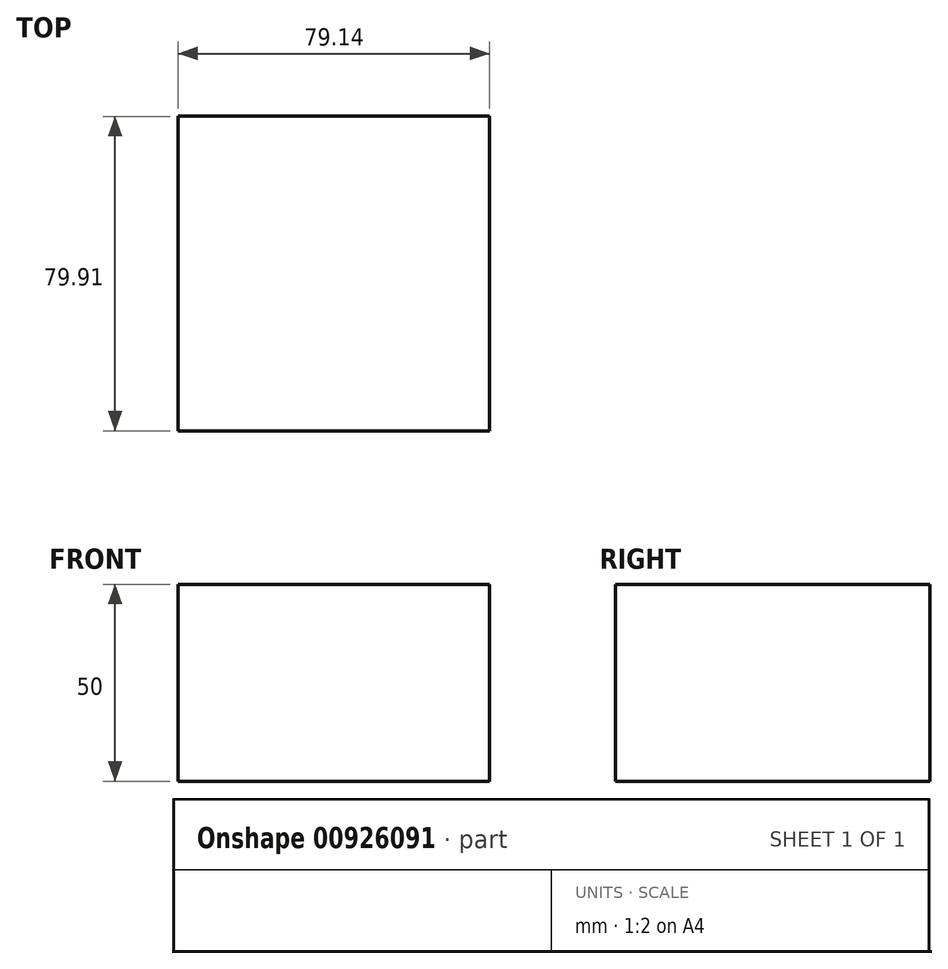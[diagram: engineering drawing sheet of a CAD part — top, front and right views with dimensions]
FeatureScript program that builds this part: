
annotation { "Feature Type Name" : "Feature", "Feature Type Description" : "" }
export const myFeature = defineFeature(function(context is Context, id is Id, definition is map)
    precondition{}
    {
        {
            var Q0;
            Q0=qCreatedBy(makeId("Top.planeOp"),FACE);
            var sketch = newSketch(context, id + "F0", { "sketchPlane" : qUnion([Q0])});
            skLineSegment(sketch, "E0.bottom", {"start": v(9.99, -15.03) * mm, "end": v(10.38, -15.03) * mm});
            skLineSegment(sketch, "E0.top", {"start": v(9.99, -19.69) * mm, "end": v(10.38, -19.69) * mm});
            skLineSegment(sketch, "E1.bottom", {"start": v(31.9, -28.6) * mm, "end": v(-47.23, -28.6) * mm});
            skLineSegment(sketch, "E1.top", {"start": v(31.9, 51.3) * mm, "end": v(-47.23, 51.3) * mm});
            skLineSegment(sketch, "E1.left", {"start": v(31.9, -28.6) * mm, "end": v(31.9, 51.3) * mm});
            skLineSegment(sketch, "E1.right", {"start": v(-47.23, -28.6) * mm, "end": v(-47.23, 51.3) * mm});
            skPoint(sketch, "E1.middle", {"position": v(-7.66, 11.35) * mm});
            skSolve(sketch);
        }
        {
            var Q0;
            Q0 = qSketchRegion(id + "F0", true);
            extrude(context, id + "F1", {"entities" : qUnion([Q0]), "depth" : 25 * mm, "offsetDistance" : 25 * mm});
        }
        {
            var Q0;
            Q0=makeQuery(id+"F1.opExtrude","CAP_FACE",FACE,{"disambiguationData":[OSD([sQuery(id+"F0.wireOp",EDGE,"E1.bottom"),sQuery(id+"F0.wireOp",EDGE,"E1.top"),sQuery(id+"F0.wireOp",EDGE,"E1.left"),sQuery(id+"F0.wireOp",EDGE,"E1.right")])],"isStart":false});
            extrude(context, id + "F2", {"entities" : qUnion([Q0]), "operationType" : NewBodyOperationType.ADD, "depth" : 25 * mm, "offsetDistance" : 25 * mm});
        }
    });
